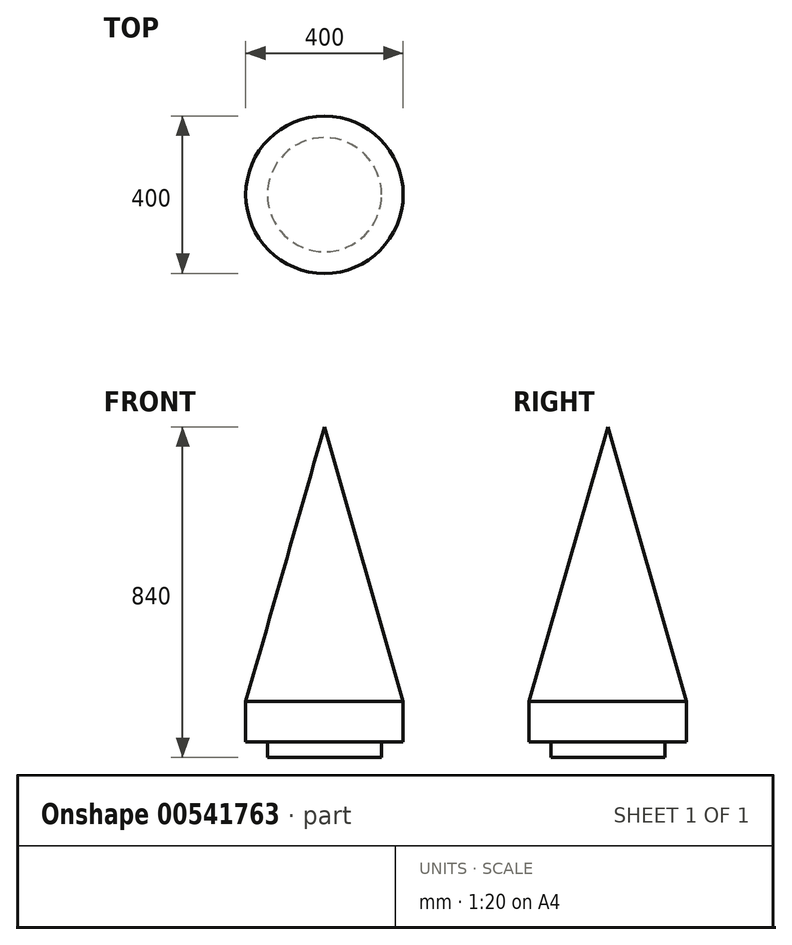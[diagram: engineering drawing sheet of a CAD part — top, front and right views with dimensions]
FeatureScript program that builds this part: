
annotation { "Feature Type Name" : "Feature", "Feature Type Description" : "" }
export const myFeature = defineFeature(function(context is Context, id is Id, definition is map)
    precondition{}
    {
        {
            var Q0;
            Q0=qCreatedBy(makeId("Top.planeOp"),FACE);
            var sketch = newSketch(context, id + "F0", { "sketchPlane" : qUnion([Q0])});
            skCircle(sketch, "E0", {"center": v(0, 0) * mm, "radius": 200 * mm});
            skSolve(sketch);
        }
        {
            var Q0;
            Q0 = qSketchRegion(id + "F0", true);
            extrude(context, id + "F1", {"entities" : qUnion([Q0]), "depth" : 800 * mm, "offsetDistance" : 25 * mm});
        }
        {
            var Q0;
            Q0=makeQuery(id+"F1.opExtrude","CAP_FACE",FACE,{"disambiguationData":[OSD([sQuery(id+"F0.wireOp",EDGE,"E0")])],"isStart":false});
            chamfer(context, id + "F2", {"entities" : qUnion([Q0]), "chamferType" : ChamferType.OFFSET_ANGLE, "width" : 200 * mm, "oppositeDirection" : false, "angle" : 74 * degree, "tangentPropagation" : true});
        }
        {
            var Q0;
            Q0=makeQuery(id+"F1.opExtrude","CAP_FACE",FACE,{"disambiguationData":[OSD([sQuery(id+"F0.wireOp",EDGE,"E0")])],"isStart":true});
            var sketch = newSketch(context, id + "F3", { "sketchPlane" : qUnion([Q0])});
            skCircle(sketch, "E1", {"center": v(0, 0) * mm, "radius": 145 * mm});
            skSolve(sketch);
        }
        {
            var Q0;
            Q0=makeQuery(id+"F3.imprint","IMPRINT",FACE,{"disambiguationData":[TD([[makeQuery(id+"F3.imprint","IMPRINT",EDGE,{"derivedFrom":sQuery(id+"F3.wireOp",EDGE,"E1")}),1.0]])]});
            extrude(context, id + "F4", {"entities" : qUnion([Q0]), "operationType" : NewBodyOperationType.ADD, "depth" : 40 * mm, "offsetDistance" : 25 * mm});
        }
    });
